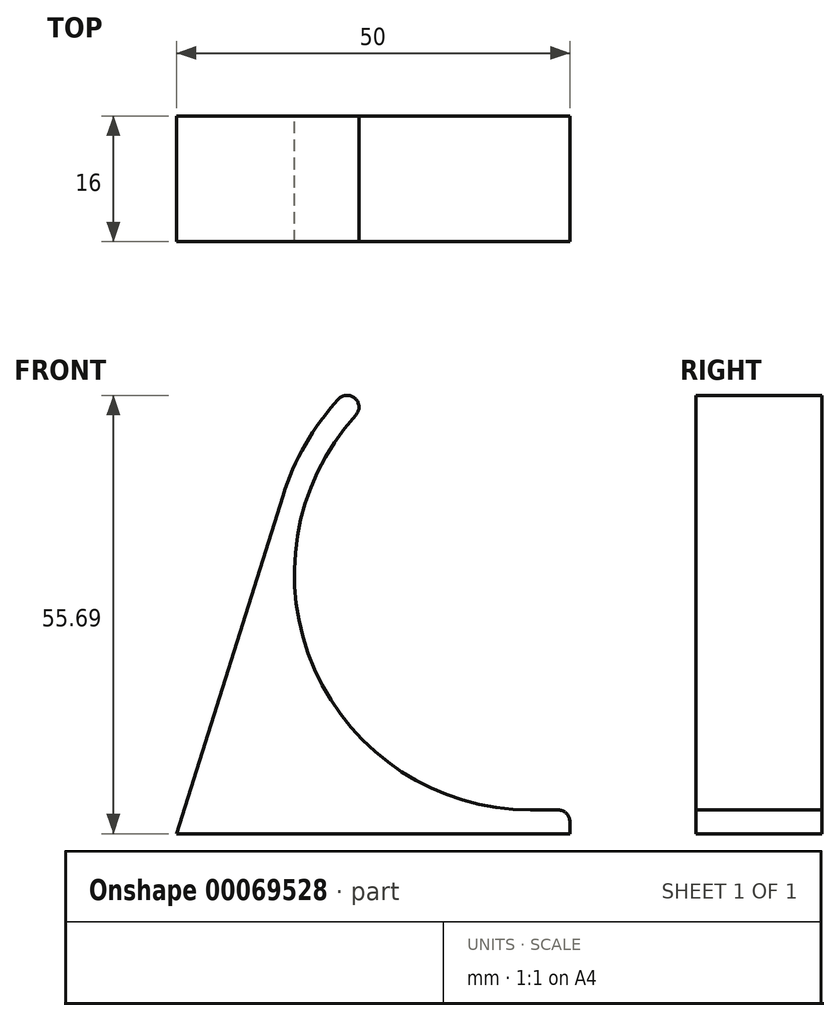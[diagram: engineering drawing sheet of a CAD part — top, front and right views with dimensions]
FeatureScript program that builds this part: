
annotation { "Feature Type Name" : "Feature", "Feature Type Description" : "" }
export const myFeature = defineFeature(function(context is Context, id is Id, definition is map)
    precondition{}
    {
        {
            var Q0;
            Q0=qCreatedBy(makeId("Front.planeOp"),FACE);
            var sketch = newSketch(context, id + "F0", { "sketchPlane" : qUnion([Q0])});
            skCircle(sketch, "E0", {"center": v(0, 0) * mm, "radius": 30 * mm});
            skLineSegment(sketch, "E1", {"start": v(0, 0) * mm, "end": v(0, -33) * mm, "construction": true});
            skLineSegment(sketch, "E2", {"start": v(-45, -33) * mm, "end": v(5, -33) * mm});
            skCircle(sketch, "E3", {"center": v(0, 0) * mm, "radius": 33 * mm});
            skLineSegment(sketch, "E4", {"start": v(0, -30) * mm, "end": v(5, -30) * mm});
            skLineSegment(sketch, "E5", {"start": v(5, -30) * mm, "end": v(5, -33) * mm});
            skLineSegment(sketch, "E6", {"start": v(-45, -33) * mm, "end": v(-31.47, 9.92) * mm});
            skLineSegment(sketch, "E7", {"start": v(0, 0) * mm, "end": v(-23.33, 23.33) * mm});
            skLineSegment(sketch, "E8", {"start": v(0, 0) * mm, "end": v(-33, 0) * mm, "construction": true});
            skSolve(sketch);
        }
        {
            var Q0;
            {var subQ0=sQuery(id+"F0.wireOp",EDGE,"E6");Q0=makeQuery(id+"F0.imprint","IMPRINT",FACE,{"disambiguationData":[TD([[makeQuery(id+"F0.imprint","IMPRINT",EDGE,{"derivedFrom":subQ0}),-1.0]])]});}
            var Q1;
            {var subQ0=sQuery(id+"F0.wireOp",EDGE,"E5");Q1=makeQuery(id+"F0.imprint","IMPRINT",FACE,{"disambiguationData":[TD([[makeQuery(id+"F0.imprint","IMPRINT",EDGE,{"derivedFrom":subQ0}),-1.0]])]});}
            var Q2;
            {var subQ3=sQuery(id+"F0.wireOp",EDGE,"E4");var subQ7=sQuery(id+"F0.wireOp",EDGE,"E0");var subQ8=makeQuery(id+"F0.imprint","INTERSECT",VERTEX,{"derivedFrom":[subQ7,subQ3]});Q2=makeQuery(id+"F0.imprint","IMPRINT",FACE,{"disambiguationData":[TD([[makeQuery(id+"F0.imprint","IMPRINT",EDGE,{"disambiguationData":[TD([[subQ8,1.0]])],"derivedFrom":subQ7}),-1.0]])]});}
            extrude(context, id + "F1", {"entities" : qUnion([Q0, Q1, Q2]), "depth" : 16 * mm, "offsetDistance" : 25 * mm});
        }
        {
            var Q0;
            Q0=makeQuery(id+"F1.opExtrude","SWEPT_EDGE",EDGE,{"disambiguationData":[OSD([sQuery(id+"F0.wireOp",EDGE,"E0"),sQuery(id+"F0.wireOp",EDGE,"E7")])]});
            var Q1;
            Q1=makeQuery(id+"F1.opExtrude","SWEPT_EDGE",EDGE,{"disambiguationData":[OSD([sQuery(id+"F0.wireOp",EDGE,"E3"),sQuery(id+"F0.wireOp",EDGE,"E7")])]});
            var Q2;
            Q2=makeQuery(id+"F1.opExtrude","SWEPT_EDGE",EDGE,{"disambiguationData":[OSD([sQuery(id+"F0.wireOp",EDGE,"E4"),sQuery(id+"F0.wireOp",EDGE,"E5")])]});
            fillet(context, id + "F2", {"entities" : qUnion([Q0, Q1, Q2]), "tangentPropagation" : true, "radius" : 1.5 * mm, "defaultsChanged" : false, "vertexSettings" : [], "allowEdgeOverflow" : false});
        }
    });
